# Revit family: Damper-Cable_Operated-Carnes-Round-Single_Blade_FQBA
name_source: partatom
category: Duct Accessories
revit_build: Autodesk Revit Architecture 2012 (Build: 20110916_2132(x64)
units: mm (PartAtom-declared; Revit-internal decimal feet)

## types (1)
- FQBA
    04 CSI = 08 91 00
    95 CSI = 10200
    Assembly Code = D3090700
    Bearing Length = 4"
    Blade Material = Steel - Carnes – Galvanized
    Catalog URL = http://www.carnes.com
    Connector Descriptor 1 = Duct Connection 1
    Connector Descriptor 2 = Duct Connection 2
    Damper Air Flow = 0 CFM
    Depth = 8"
    Description = Cable Operated Dampers
    Frame Material = Steel - Carnes – Galvanized
    Manufacturer = Carnes Company
    Manufacturer Fax = 608-845-6470
    Model = FQBA
    Pressure Drop = 0.00 Pa
    Product Line = Cable Operated Dampers
    Product Page URL = http://www.carnes.com
    Specifications URL = http://www.carnes.com
    Subcategory = Louvers and Dampers
    URL = http://www.carnes.com
    ecoScorecard Product Page = http://www.ecoscorecard.com

## geometry (parser evidence)
native form markers: Sweep x1
no freeform markers — native parametric forms only
